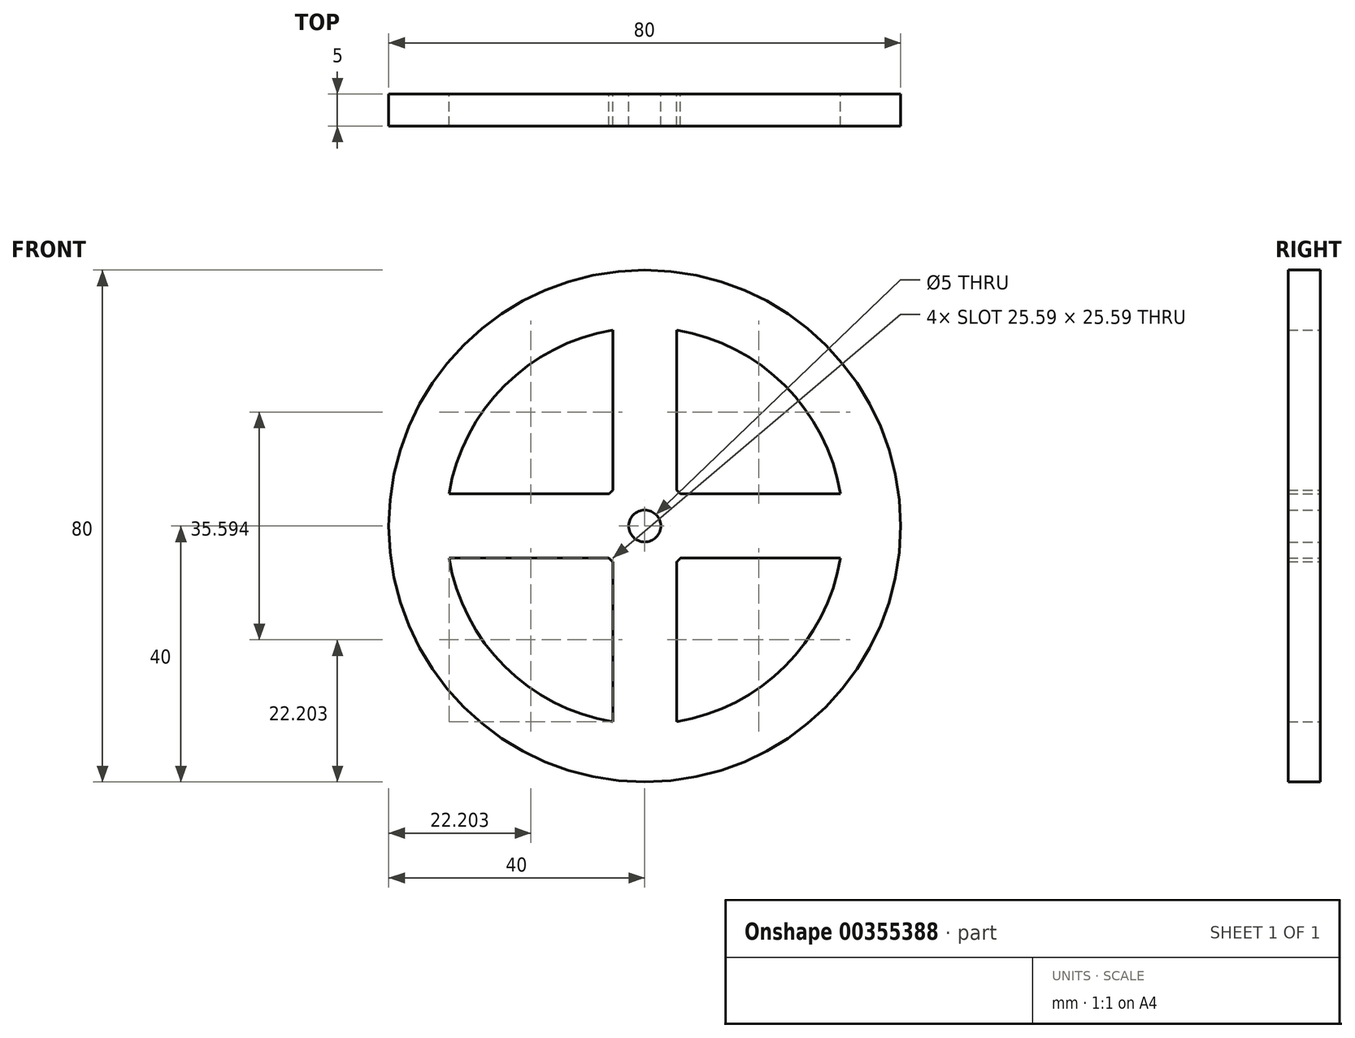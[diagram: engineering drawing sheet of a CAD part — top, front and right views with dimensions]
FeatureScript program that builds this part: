
annotation { "Feature Type Name" : "Feature", "Feature Type Description" : "" }
export const myFeature = defineFeature(function(context is Context, id is Id, definition is map)
    precondition{}
    {
        {
            var Q0;
            Q0=qCreatedBy(makeId("Front.planeOp"),FACE);
            var sketch = newSketch(context, id + "F0", { "sketchPlane" : qUnion([Q0])});
            skCircle(sketch, "E0", {"center": v(0, 0) * mm, "radius": 40 * mm});
            skArc(sketch, "E1", {"start": v(-30.6, -5) * mm, "mid": v(-21.92, -21.92) * mm, "end": v(-5, -30.6) * mm});
            skArc(sketch, "E2", {"start": v(-5.6, -5) * mm, "mid": v(-5.3, -5.3) * mm, "end": v(-5, -5.6) * mm});
            skCircle(sketch, "E3", {"center": v(0, 0) * mm, "radius": 2.5 * mm});
            skLineSegment(sketch, "E4", {"start": v(0, 0) * mm, "end": v(2.5, 0) * mm});
            skLineSegment(sketch, "E5", {"start": v(0, 0) * mm, "end": v(0, -2.5) * mm});
            skLineSegment(sketch, "E6", {"start": v(-7.5, 0) * mm, "end": v(-31, 0) * mm, "construction": true});
            skLineSegment(sketch, "E7.0", {"start": v(-5, 5.6) * mm, "end": v(-5, 30.6) * mm});
            skLineSegment(sketch, "E8.0", {"start": v(5, 5.6) * mm, "end": v(5, 30.6) * mm});
            skLineSegment(sketch, "E9.0", {"start": v(-5.6, 5) * mm, "end": v(-30.6, 5) * mm});
            skLineSegment(sketch, "E10.0", {"start": v(-5.6, -5) * mm, "end": v(-30.6, -5) * mm});
            skLineSegment(sketch, "E11.0", {"start": v(-5, -5.6) * mm, "end": v(-5, -30.6) * mm});
            skLineSegment(sketch, "E12.0", {"start": v(5, -5.6) * mm, "end": v(5, -30.6) * mm});
            skLineSegment(sketch, "E13.0", {"start": v(5.6, 5) * mm, "end": v(30.6, 5) * mm});
            skLineSegment(sketch, "E14.0", {"start": v(5.6, -5) * mm, "end": v(30.6, -5) * mm});
            skLineSegment(sketch, "E15.trimOffspring", {"start": v(-5, 39.69) * mm, "end": v(-5, 40) * mm});
            skLineSegment(sketch, "E16.trimOffspring", {"start": v(5, 39.69) * mm, "end": v(5, 40) * mm});
            skLineSegment(sketch, "E17.trimOffspring", {"start": v(39.69, 5) * mm, "end": v(40, 5) * mm});
            skLineSegment(sketch, "E18.trimOffspring", {"start": v(39.69, -5) * mm, "end": v(40, -5) * mm});
            skLineSegment(sketch, "E19.trimOffspring", {"start": v(5, -39.69) * mm, "end": v(5, -40) * mm});
            skLineSegment(sketch, "E20.trimOffspring", {"start": v(-5, -39.69) * mm, "end": v(-5, -40) * mm});
            skLineSegment(sketch, "E21.trimOffspring", {"start": v(-39.69, 5) * mm, "end": v(-40, 5) * mm});
            skLineSegment(sketch, "E22.trimOffspring", {"start": v(-39.69, -5) * mm, "end": v(-40, -5) * mm});
            skArc(sketch, "E23.trimOffspring", {"start": v(-5, 30.6) * mm, "mid": v(-21.92, 21.92) * mm, "end": v(-30.6, 5) * mm});
            skArc(sketch, "E24.trimOffspring", {"start": v(30.6, 5) * mm, "mid": v(21.92, 21.92) * mm, "end": v(5, 30.6) * mm});
            skArc(sketch, "E25.trimOffspring", {"start": v(5, -30.6) * mm, "mid": v(21.92, -21.92) * mm, "end": v(30.6, -5) * mm});
            skArc(sketch, "E26.trimOffspring", {"start": v(-5, 5.6) * mm, "mid": v(-5.3, 5.3) * mm, "end": v(-5.6, 5) * mm});
            skPoint(sketch, "E27.orphan", {"position": v(-2.5, 0) * mm});
            skLineSegment(sketch, "E28.trimOffspring", {"start": v(0, -7.5) * mm, "end": v(0, -31) * mm, "construction": true});
            skLineSegment(sketch, "E29.trimOffspring", {"start": v(7.5, 0) * mm, "end": v(31, 0) * mm, "construction": true});
            skArc(sketch, "E30.trimOffspring", {"start": v(5.6, 5) * mm, "mid": v(5.3, 5.3) * mm, "end": v(5, 5.6) * mm});
            skArc(sketch, "E31.trimOffspring", {"start": v(5, -5.6) * mm, "mid": v(5.3, -5.3) * mm, "end": v(5.6, -5) * mm});
            skLineSegment(sketch, "E32", {"start": v(0, 36.14) * mm, "end": v(0, 0) * mm, "construction": true});
            skLineSegment(sketch, "E33.0", {"start": v(5, 30.6) * mm, "end": v(5, 5.6) * mm});
            skLineSegment(sketch, "E34.0", {"start": v(-5, 30.6) * mm, "end": v(-5, 5.6) * mm});
            skSolve(sketch);
        }
        {
            var Q0;
            Q0 = qSketchRegion(id + "F0", true);
            extrude(context, id + "F1", {"entities" : qUnion([Q0]), "endBound" : BoundingType.SYMMETRIC, "depth" : 5 * mm});
        }
    });
